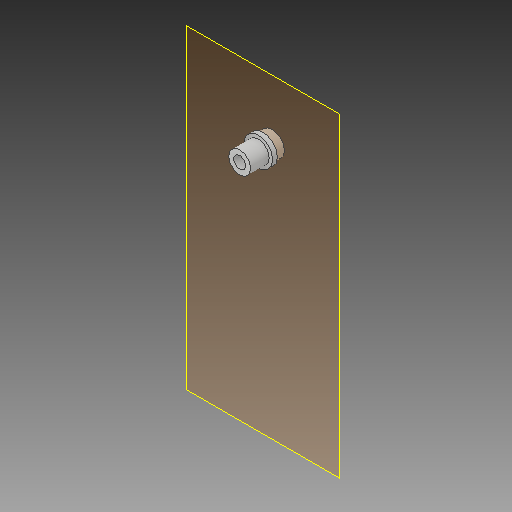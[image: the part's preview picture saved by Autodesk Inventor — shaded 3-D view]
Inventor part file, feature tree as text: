
AUTODESK INVENTOR PART (.ipt)
format: ipt  version: 2018.3 (Build 223284000, 284)  size: 108,032 bytes
history: native  units: mm
features: other x7, extrude x4, sketch x4, reference x1
ambient origin geometry x8: Origin, YZ Plane, XZ Plane, XY Plane, X Axis, Y Axis, Z Axis, Center Point
bodies: Body1 (feature_tree)
feature tree (16):
  other  "Твердое тело1"
  other  "РабПлоскость1"
  extrude  "Выдавливание1"  Depth=10.0mm TaperAngle=0.0deg
  extrude  "Выдавливание2"  Depth=31.0mm
  extrude  "Выдавливание3"  Depth=5.2mm TaperAngle=0.0deg
  extrude  "Выдавливание4"  Depth=23.8mm
  sketch  "Эскиз1"
  sketch  "Эскиз2"
  sketch  "Эскиз3"
  sketch  "Эскиз4"
  reference  "Ссылка2"
  other  "<userpath>\GoogleDrive\My_project\Механика\Кофемашина\Inventor\Сборка.iam"
  other  "Сборка.iam"
  other  "Зубчатая передача:1"
  other  "Большая шестерня:1"
  other  "Основание:1"
